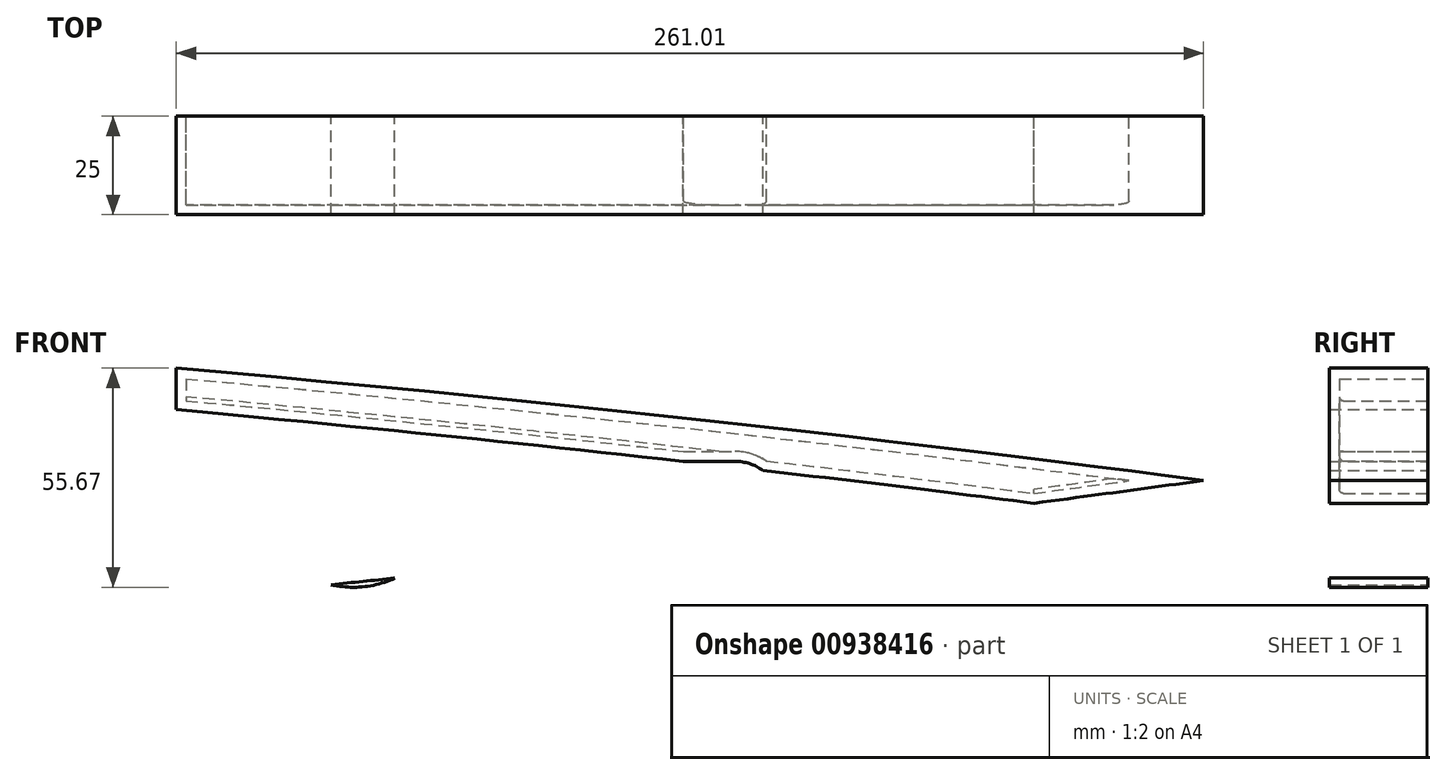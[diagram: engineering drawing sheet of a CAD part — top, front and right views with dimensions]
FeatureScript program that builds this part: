
annotation { "Feature Type Name" : "Feature", "Feature Type Description" : "" }
export const myFeature = defineFeature(function(context is Context, id is Id, definition is map)
    precondition{}
    {
        {
            var Q0;
            Q0=qCreatedBy(makeId("Front.planeOp"),FACE);
            var sketch = newSketch(context, id + "F0", { "sketchPlane" : qUnion([Q0])});
            skLineSegment(sketch, "E0", {"start": v(0, 0) * mm, "end": v(830, 0) * mm});
            skLineSegment(sketch, "E1", {"start": v(23.53, 0) * mm, "end": v(23.53, 22.98) * mm, "construction": true});
            skLineSegment(sketch, "E2", {"start": v(30.64, 0) * mm, "end": v(30.64, 25.86) * mm, "construction": true});
            skLineSegment(sketch, "E3", {"start": v(38.65, 0) * mm, "end": v(38.65, 28.62) * mm, "construction": true});
            skLineSegment(sketch, "E4", {"start": v(47.54, 0) * mm, "end": v(47.54, 31.24) * mm, "construction": true});
            skLineSegment(sketch, "E5", {"start": v(57.28, 0) * mm, "end": v(57.28, 33.72) * mm, "construction": true});
            skLineSegment(sketch, "E6", {"start": v(67.86, 0) * mm, "end": v(67.86, 36.05) * mm, "construction": true});
            skLineSegment(sketch, "E7", {"start": v(79.26, 0) * mm, "end": v(79.26, 38.22) * mm, "construction": true});
            skLineSegment(sketch, "E8", {"start": v(91.44, 0) * mm, "end": v(91.44, 40.22) * mm, "construction": true});
            skLineSegment(sketch, "E9", {"start": v(104.37, 0) * mm, "end": v(104.37, 42.04) * mm, "construction": true});
            skLineSegment(sketch, "E10", {"start": v(118.03, 0) * mm, "end": v(118.03, 43.68) * mm, "construction": true});
            skLineSegment(sketch, "E11", {"start": v(132.38, 0) * mm, "end": v(132.38, 45.13) * mm, "construction": true});
            skLineSegment(sketch, "E12", {"start": v(147.4, 0) * mm, "end": v(147.4, 46.38) * mm, "construction": true});
            skLineSegment(sketch, "E13", {"start": v(163.03, 0) * mm, "end": v(163.03, 47.45) * mm, "construction": true});
            skLineSegment(sketch, "E14", {"start": v(179.25, 0) * mm, "end": v(179.25, 48.31) * mm, "construction": true});
            skLineSegment(sketch, "E15", {"start": v(196.03, 0) * mm, "end": v(196.03, 48.98) * mm, "construction": true});
            skLineSegment(sketch, "E16", {"start": v(213.32, 0) * mm, "end": v(213.32, 49.45) * mm, "construction": true});
            skLineSegment(sketch, "E17", {"start": v(231.08, 0) * mm, "end": v(231.08, 49.73) * mm, "construction": true});
            skLineSegment(sketch, "E18", {"start": v(249.26, 0) * mm, "end": v(249.26, 49.81) * mm, "construction": true});
            skLineSegment(sketch, "E19", {"start": v(267.84, 0) * mm, "end": v(267.84, 49.72) * mm, "construction": true});
            skLineSegment(sketch, "E20", {"start": v(0.48, 0) * mm, "end": v(0.48, 3.54) * mm, "construction": true});
            skLineSegment(sketch, "E21", {"start": v(1.94, 0) * mm, "end": v(1.94, 7) * mm, "construction": true});
            skLineSegment(sketch, "E22", {"start": v(4.35, 0) * mm, "end": v(4.35, 10.38) * mm, "construction": true});
            skLineSegment(sketch, "E23", {"start": v(7.73, 0) * mm, "end": v(7.73, 13.67) * mm, "construction": true});
            skLineSegment(sketch, "E24", {"start": v(12.06, 0) * mm, "end": v(12.06, 16.87) * mm, "construction": true});
            skLineSegment(sketch, "E25", {"start": v(17.33, 0) * mm, "end": v(17.33, 19.98) * mm, "construction": true});
            skLineSegment(sketch, "E26", {"start": v(286.76, 0) * mm, "end": v(286.76, 49.45) * mm, "construction": true});
            skLineSegment(sketch, "E27", {"start": v(305.98, 0) * mm, "end": v(305.98, 49) * mm, "construction": true});
            skLineSegment(sketch, "E28", {"start": v(325.45, 0) * mm, "end": v(325.45, 48.4) * mm, "construction": true});
            skLineSegment(sketch, "E29", {"start": v(345.13, 0) * mm, "end": v(345.13, 47.64) * mm, "construction": true});
            skLineSegment(sketch, "E30", {"start": v(364.98, 0) * mm, "end": v(364.98, 46.75) * mm, "construction": true});
            skLineSegment(sketch, "E31", {"start": v(384.94, 0) * mm, "end": v(384.94, 45.71) * mm, "construction": true});
            skLineSegment(sketch, "E32", {"start": v(404.97, 0) * mm, "end": v(404.97, 44.56) * mm, "construction": true});
            skLineSegment(sketch, "E33", {"start": v(425.03, 0) * mm, "end": v(425.03, 43.3) * mm, "construction": true});
            skLineSegment(sketch, "E34", {"start": v(445.06, 0) * mm, "end": v(445.06, 41.93) * mm, "construction": true});
            skLineSegment(sketch, "E35", {"start": v(465.02, 0) * mm, "end": v(465.02, 40.47) * mm, "construction": true});
            skLineSegment(sketch, "E36", {"start": v(484.87, 0) * mm, "end": v(484.87, 38.94) * mm, "construction": true});
            skLineSegment(sketch, "E37", {"start": v(504.55, 0) * mm, "end": v(504.55, 37.33) * mm, "construction": true});
            skLineSegment(sketch, "E38", {"start": v(524.02, 0) * mm, "end": v(524.02, 35.67) * mm, "construction": true});
            skLineSegment(sketch, "E39", {"start": v(543.24, 0) * mm, "end": v(543.24, 33.96) * mm, "construction": true});
            skLineSegment(sketch, "E40", {"start": v(562.16, 0) * mm, "end": v(562.16, 32.21) * mm, "construction": true});
            skLineSegment(sketch, "E41", {"start": v(580.74, 0) * mm, "end": v(580.74, 30.44) * mm, "construction": true});
            skLineSegment(sketch, "E42", {"start": v(598.92, 0) * mm, "end": v(598.92, 28.64) * mm, "construction": true});
            skLineSegment(sketch, "E43", {"start": v(633.97, 0) * mm, "end": v(633.97, 25.03) * mm, "construction": true});
            skLineSegment(sketch, "E44", {"start": v(616.68, 0) * mm, "end": v(616.68, 26.83) * mm, "construction": true});
            skLineSegment(sketch, "E45", {"start": v(650.75, 0) * mm, "end": v(650.75, 23.23) * mm, "construction": true});
            skLineSegment(sketch, "E46", {"start": v(666.97, 0) * mm, "end": v(666.97, 21.44) * mm, "construction": true});
            skLineSegment(sketch, "E47", {"start": v(682.6, 0) * mm, "end": v(682.6, 19.68) * mm, "construction": true});
            skLineSegment(sketch, "E48", {"start": v(697.62, 0) * mm, "end": v(697.62, 17.96) * mm, "construction": true});
            skLineSegment(sketch, "E49", {"start": v(711.97, 0) * mm, "end": v(711.97, 16.27) * mm, "construction": true});
            skLineSegment(sketch, "E50", {"start": v(725.63, 0) * mm, "end": v(725.63, 14.64) * mm, "construction": true});
            skLineSegment(sketch, "E51", {"start": v(738.56, 0) * mm, "end": v(738.56, 13.06) * mm, "construction": true});
            skLineSegment(sketch, "E52", {"start": v(750.74, 0) * mm, "end": v(750.74, 11.55) * mm, "construction": true});
            skLineSegment(sketch, "E53", {"start": v(762.14, 0) * mm, "end": v(762.14, 10.11) * mm, "construction": true});
            skLineSegment(sketch, "E54", {"start": v(791.35, 0) * mm, "end": v(791.35, 6.32) * mm, "construction": true});
            skLineSegment(sketch, "E55", {"start": v(799.36, 0) * mm, "end": v(799.36, 5.25) * mm, "construction": true});
            skLineSegment(sketch, "E56", {"start": v(806.47, 0) * mm, "end": v(806.47, 4.29) * mm, "construction": true});
            skLineSegment(sketch, "E57", {"start": v(782.46, 0) * mm, "end": v(782.46, 7.49) * mm, "construction": true});
            skLineSegment(sketch, "E58", {"start": v(812.67, 0) * mm, "end": v(812.67, 3.45) * mm, "construction": true});
            skLineSegment(sketch, "E59", {"start": v(817.94, 0) * mm, "end": v(817.94, 2.72) * mm, "construction": true});
            skLineSegment(sketch, "E60", {"start": v(822.27, 0) * mm, "end": v(822.27, 2.12) * mm, "construction": true});
            skLineSegment(sketch, "E61", {"start": v(825.65, 0) * mm, "end": v(825.65, 1.65) * mm, "construction": true});
            skLineSegment(sketch, "E62", {"start": v(828.06, 0) * mm, "end": v(828.06, 1.32) * mm, "construction": true});
            skLineSegment(sketch, "E63", {"start": v(772.72, 0) * mm, "end": v(772.72, 8.76) * mm, "construction": true});
            skLineSegment(sketch, "E64", {"start": v(829.52, 0) * mm, "end": v(829.52, 1.11) * mm, "construction": true});
            skLineSegment(sketch, "E65", {"start": v(830, 0) * mm, "end": v(830, 1.05) * mm});
            skFitSpline(sketch, "E66", {"points": [v(0, 0) * mm, v(0.48, 3.54) * mm, v(1.94, 7) * mm, v(4.35, 10.38) * mm, v(7.73, 13.67) * mm, v(12.06, 16.87) * mm, v(17.33, 19.98) * mm, v(23.53, 22.98) * mm, v(30.64, 25.86) * mm, v(38.65, 28.62) * mm, v(47.54, 31.24) * mm, v(57.28, 33.72) * mm, v(67.86, 36.05) * mm, v(79.26, 38.22) * mm, v(91.44, 40.22) * mm, v(104.37, 42.04) * mm, v(118.03, 43.68) * mm, v(132.38, 45.13) * mm, v(147.4, 46.39) * mm, v(163.03, 47.45) * mm, v(179.25, 48.31) * mm, v(196.03, 48.98) * mm, v(213.32, 49.45) * mm, v(231.08, 49.73) * mm, v(249.26, 49.81) * mm, v(267.84, 49.72) * mm, v(286.76, 49.45) * mm, v(305.98, 49) * mm, v(325.45, 48.4) * mm, v(345.13, 47.64) * mm, v(364.98, 46.75) * mm, v(384.94, 45.71) * mm, v(404.97, 44.56) * mm, v(425.03, 43.3) * mm, v(445.06, 41.93) * mm, v(465.02, 40.47) * mm, v(484.87, 38.94) * mm, v(504.55, 37.33) * mm, v(524.02, 35.67) * mm, v(543.24, 33.96) * mm, v(562.16, 32.21) * mm, v(580.74, 30.44) * mm, v(598.92, 28.64) * mm, v(616.68, 26.83) * mm, v(633.97, 25.03) * mm, v(650.75, 23.23) * mm, v(666.97, 21.44) * mm, v(682.6, 19.68) * mm, v(697.62, 17.96) * mm, v(711.97, 16.27) * mm, v(725.63, 14.64) * mm, v(738.56, 13.06) * mm, v(750.74, 11.55) * mm, v(762.14, 10.11) * mm, v(772.72, 8.76) * mm, v(782.46, 7.49) * mm, v(791.35, 6.32) * mm, v(799.36, 5.25) * mm, v(806.47, 4.29) * mm, v(812.67, 3.45) * mm, v(817.94, 2.72) * mm, v(822.27, 2.12) * mm, v(825.65, 1.65) * mm, v(828.06, 1.32) * mm, v(829.52, 1.11) * mm, v(830, 1.05) * mm], "startDerivative": vector(34.1, 427.03) * mm, "endDerivative": vector(137.1, -19.25) * mm});
            skFitSpline(sketch, "E67.MirrorCS", {"points": [v(0, 0) * mm, v(0.48, -3.54) * mm, v(1.94, -7) * mm, v(4.35, -10.38) * mm, v(7.73, -13.67) * mm, v(12.06, -16.87) * mm, v(17.33, -19.98) * mm, v(23.53, -22.98) * mm, v(30.64, -25.86) * mm, v(38.65, -28.62) * mm, v(47.54, -31.24) * mm, v(57.28, -33.72) * mm, v(67.86, -36.05) * mm, v(79.26, -38.22) * mm, v(91.44, -40.22) * mm, v(104.37, -42.04) * mm, v(118.03, -43.68) * mm, v(132.38, -45.13) * mm, v(147.4, -46.39) * mm, v(163.03, -47.45) * mm, v(179.25, -48.31) * mm, v(196.03, -48.98) * mm, v(213.32, -49.45) * mm, v(231.08, -49.73) * mm, v(249.26, -49.81) * mm, v(267.84, -49.72) * mm, v(286.76, -49.45) * mm, v(305.98, -49) * mm, v(325.45, -48.4) * mm, v(345.13, -47.64) * mm, v(364.98, -46.75) * mm, v(384.94, -45.71) * mm, v(404.97, -44.56) * mm, v(425.03, -43.3) * mm, v(445.06, -41.93) * mm, v(465.02, -40.47) * mm, v(484.87, -38.94) * mm, v(504.55, -37.33) * mm, v(524.02, -35.67) * mm, v(543.24, -33.96) * mm, v(562.16, -32.21) * mm, v(580.74, -30.44) * mm, v(598.92, -28.64) * mm, v(616.68, -26.83) * mm, v(633.97, -25.03) * mm, v(650.75, -23.23) * mm, v(666.97, -21.44) * mm, v(682.6, -19.68) * mm, v(697.62, -17.96) * mm, v(711.97, -16.27) * mm, v(725.63, -14.64) * mm, v(738.56, -13.06) * mm, v(750.74, -11.55) * mm, v(762.14, -10.11) * mm, v(772.72, -8.76) * mm, v(782.46, -7.49) * mm, v(791.35, -6.32) * mm, v(799.36, -5.25) * mm, v(806.47, -4.29) * mm, v(812.67, -3.45) * mm, v(817.94, -2.72) * mm, v(822.27, -2.12) * mm, v(825.65, -1.65) * mm, v(828.06, -1.32) * mm, v(829.52, -1.11) * mm, v(830, -1.05) * mm], "startDerivative": vector(34.1, -427.03) * mm, "endDerivative": vector(137.1, 19.25) * mm});
            skLineSegment(sketch, "E68.MirrorCS", {"start": v(830, 0) * mm, "end": v(830, -1.05) * mm});
            skLineSegment(sketch, "E69", {"start": v(163.03, 47.45) * mm, "end": v(163.03, -47.45) * mm});
            skLineSegment(sketch, "E70", {"start": v(204.25, -49.23) * mm, "end": v(204.25, -33.23) * mm});
            skLineSegment(sketch, "E71", {"start": v(204.25, -33.23) * mm, "end": v(179.25, -33.23) * mm});
            skLineSegment(sketch, "E72", {"start": v(179.25, -33.23) * mm, "end": v(179.25, 33.23) * mm});
            skLineSegment(sketch, "E73", {"start": v(179.25, 33.23) * mm, "end": v(204.25, 33.23) * mm});
            skLineSegment(sketch, "E74", {"start": v(204.25, 33.23) * mm, "end": v(204.25, 49.23) * mm});
            skLineSegment(sketch, "E75", {"start": v(524.02, 35.67) * mm, "end": v(524.02, -35.67) * mm});
            skLineSegment(sketch, "E76", {"start": v(479.55, -39.36) * mm, "end": v(479.55, -23.36) * mm});
            skLineSegment(sketch, "E77", {"start": v(479.55, -23.36) * mm, "end": v(504.55, -23.36) * mm});
            skLineSegment(sketch, "E78", {"start": v(504.55, -23.36) * mm, "end": v(504.55, 23.36) * mm});
            skLineSegment(sketch, "E79", {"start": v(504.55, 23.36) * mm, "end": v(479.55, 23.36) * mm});
            skLineSegment(sketch, "E80", {"start": v(479.55, 23.36) * mm, "end": v(479.55, 39.36) * mm});
            skEllipse(sketch, "E81", {"center": v(240.25, 0) * mm, "majorRadius": 36.5 * mm, "minorRadius": 30 * mm, "majorAxis": v(1, 0)});
            skEllipse(sketch, "E82.1.0.0", {"center": v(333.25, 0) * mm, "majorRadius": 36.5 * mm, "minorRadius": 30 * mm, "majorAxis": v(1, 0)});
            skLineSegment(sketch, "E82.direction1", {"start": v(240.25, 0) * mm, "end": v(333.25, 0) * mm, "construction": true});
            skEllipse(sketch, "E83", {"center": v(425.03, 0) * mm, "majorRadius": 28 * mm, "minorRadius": 36.5 * mm, "majorAxis": v(0, -1)});
            skFitSpline(sketch, "E84.0", {"points": [v(19.9, 0) * mm, v(19.93, 0.28) * mm, v(19.97, 0.77) * mm, v(20.03, 1.33) * mm, v(20.07, 1.63) * mm, v(20.1, 1.78) * mm, v(20.12, 1.85) * mm, v(20.12, 1.88) * mm, v(20.13, 1.92) * mm, v(20.16, 1.99) * mm, v(20.2, 2.1) * mm, v(20.28, 2.3) * mm, v(20.43, 2.58) * mm, v(20.63, 2.94) * mm, v(20.87, 3.32) * mm, v(21.13, 3.7) * mm, v(21.53, 4.23) * mm, v(22.12, 4.91) * mm, v(22.98, 5.8) * mm, v(24.01, 6.71) * mm, v(25.19, 7.65) * mm, v(26.5, 8.6) * mm, v(28.4, 9.86) * mm, v(31.06, 11.42) * mm, v(34.64, 13.25) * mm, v(38.55, 15) * mm, v(44.15, 17.24) * mm, v(51.77, 19.86) * mm, v(61.74, 22.7) * mm, v(72.4, 25.26) * mm, v(83.62, 27.56) * mm, v(95.37, 29.62) * mm, v(107.56, 31.45) * mm, v(124.36, 33.6) * mm, v(146.26, 35.8) * mm, v(173.73, 37.69) * mm, v(202.17, 38.91) * mm, v(231.43, 39.53) * mm, v(261.35, 39.6) * mm, v(291.8, 39.18) * mm, v(322.69, 38.31) * mm, v(364.28, 36.62) * mm, v(416.8, 33.63) * mm, v(479.93, 28.95) * mm, v(531.98, 24.38) * mm, v(572.9, 20.44) * mm, v(603.14, 17.37) * mm, v(632.79, 14.2) * mm, v(661.73, 10.99) * mm, v(689.84, 7.73) * mm, v(716.93, 4.47) * mm, v(738.52, 1.78) * mm, v(755.07, -0.33) * mm, v(767.08, -1.9) * mm, v(778.65, -3.43) * mm, v(789.72, -4.91) * mm, v(800.24, -6.35) * mm, v(810.11, -7.7) * mm, v(817.7, -8.77) * mm, v(823.32, -9.57) * mm, v(826.6, -10.03) * mm, v(829.07, -10.39) * mm, v(830.84, -10.64) * mm, v(832.51, -10.88) * mm, v(834.08, -11.1) * mm, v(835.26, -11.27) * mm, v(836.14, -11.4) * mm, v(836.78, -11.5) * mm, v(837.37, -11.58) * mm, v(837.78, -11.64) * mm, v(838.05, -11.68) * mm, v(838.28, -11.71) * mm, v(838.4, -11.73) * mm, v(838.5, -11.74) * mm]});
            skFitSpline(sketch, "E85.MirrorCS", {"points": [v(19.9, 0) * mm, v(19.93, -0.28) * mm, v(19.97, -0.77) * mm, v(20.03, -1.33) * mm, v(20.08, -1.63) * mm, v(20.1, -1.78) * mm, v(20.12, -1.85) * mm, v(20.13, -1.87) * mm, v(20.14, -1.92) * mm, v(20.16, -1.99) * mm, v(20.2, -2.1) * mm, v(20.29, -2.29) * mm, v(20.44, -2.58) * mm, v(20.64, -2.94) * mm, v(20.88, -3.31) * mm, v(21.15, -3.7) * mm, v(21.55, -4.22) * mm, v(22.13, -4.9) * mm, v(23, -5.78) * mm, v(24.04, -6.7) * mm, v(25.22, -7.63) * mm, v(26.52, -8.57) * mm, v(28.44, -9.83) * mm, v(31.1, -11.38) * mm, v(34.7, -13.2) * mm, v(38.6, -14.93) * mm, v(44.21, -17.15) * mm, v(51.85, -19.74) * mm, v(61.83, -22.54) * mm, v(72.49, -25.06) * mm, v(83.73, -27.32) * mm, v(95.48, -29.34) * mm, v(107.68, -31.12) * mm, v(124.49, -33.22) * mm, v(146.4, -35.32) * mm, v(173.87, -37.11) * mm, v(202.32, -38.23) * mm, v(231.57, -38.74) * mm, v(261.5, -38.7) * mm, v(291.95, -38.16) * mm, v(322.83, -37.18) * mm, v(364.42, -35.33) * mm, v(416.93, -32.14) * mm, v(480.03, -27.22) * mm, v(532.07, -22.46) * mm, v(572.98, -18.36) * mm, v(603.2, -15.18) * mm, v(632.84, -11.91) * mm, v(661.77, -8.58) * mm, v(689.86, -5.22) * mm, v(716.95, -1.86) * mm, v(738.52, 0.91) * mm, v(755.06, 3.1) * mm, v(767.06, 4.7) * mm, v(778.63, 6.27) * mm, v(789.7, 7.8) * mm, v(800.21, 9.27) * mm, v(810.08, 10.67) * mm, v(817.67, 11.77) * mm, v(823.28, 12.58) * mm, v(826.56, 13.06) * mm, v(829.03, 13.42) * mm, v(830.8, 13.68) * mm, v(832.47, 13.93) * mm, v(834.03, 14.16) * mm, v(835.21, 14.33) * mm, v(836.1, 14.46) * mm, v(836.73, 14.56) * mm, v(837.32, 14.64) * mm, v(837.73, 14.7) * mm, v(838, 14.75) * mm, v(838.23, 14.78) * mm, v(838.36, 14.8) * mm, v(838.45, 14.81) * mm]});
            skLineSegment(sketch, "E86", {"start": v(100.03, 30.3) * mm, "end": v(134.03, 30.3) * mm});
            skLineSegment(sketch, "E87", {"start": v(140.03, 24.3) * mm, "end": v(140.03, -24.26) * mm});
            skLineSegment(sketch, "E88", {"start": v(133.98, -30.26) * mm, "end": v(100.03, -29.99) * mm});
            skPoint(sketch, "E89.visualSharp", {"position": v(140.03, 30.3) * mm});
            skArc(sketch, "E89.filletArc", {"start": v(140.03, 24.3) * mm, "mid": v(138.27, 28.55) * mm, "end": v(134.03, 30.3) * mm});
            skPoint(sketch, "E90.visualSharp", {"position": v(140.03, -30.3) * mm});
            skArc(sketch, "E90.filletArc", {"start": v(133.98, -30.26) * mm, "mid": v(138.25, -28.52) * mm, "end": v(140.03, -24.26) * mm});
            skEllipse(sketch, "E91", {"center": v(569.02, 0) * mm, "majorRadius": 20 * mm, "minorRadius": 22.5 * mm, "majorAxis": v(0, -1)});
            skLineSegment(sketch, "E92.bottom", {"start": v(625.97, -12) * mm, "end": v(665.97, -12) * mm});
            skLineSegment(sketch, "E92.top", {"start": v(625.97, 12) * mm, "end": v(665.97, 12) * mm});
            skLineSegment(sketch, "E92.left", {"start": v(623.97, -10) * mm, "end": v(623.97, 10) * mm});
            skLineSegment(sketch, "E92.right", {"start": v(665.97, -12) * mm, "end": v(665.97, 12) * mm});
            skPoint(sketch, "E92.middle", {"position": v(644.97, 0) * mm});
            skArc(sketch, "E93", {"start": v(665.97, 12) * mm, "mid": v(677.97, 0) * mm, "end": v(665.97, -12) * mm});
            skPoint(sketch, "E94.visualSharp", {"position": v(623.97, 12) * mm});
            skArc(sketch, "E94.filletArc", {"start": v(625.97, 12) * mm, "mid": v(624.56, 11.41) * mm, "end": v(623.97, 10) * mm});
            skPoint(sketch, "E95.visualSharp", {"position": v(623.97, -12) * mm});
            skArc(sketch, "E95.filletArc", {"start": v(623.97, -10) * mm, "mid": v(624.56, -11.41) * mm, "end": v(625.97, -12) * mm});
            skPoint(sketch, "E96", {"position": v(276.75, 0) * mm});
            skPoint(sketch, "E97", {"position": v(296.75, 0) * mm});
            skLineSegment(sketch, "E98.bottom", {"start": v(276.26, 65.67) * mm, "end": v(297.26, 65.67) * mm});
            skLineSegment(sketch, "E98.top", {"start": v(276.26, 33.23) * mm, "end": v(297.26, 33.23) * mm});
            skLineSegment(sketch, "E98.left", {"start": v(276.26, 65.67) * mm, "end": v(276.26, 33.23) * mm});
            skLineSegment(sketch, "E98.right", {"start": v(297.26, 65.67) * mm, "end": v(297.26, 33.23) * mm});
            skPoint(sketch, "E99", {"position": v(369.75, 0) * mm});
            skPoint(sketch, "E100", {"position": v(388.53, 0) * mm});
            skLineSegment(sketch, "E101", {"start": v(379.14, 0) * mm, "end": v(379.14, 46.03) * mm, "construction": true});
            skLineSegment(sketch, "E102.bottom", {"start": v(368.64, 58.81) * mm, "end": v(389.64, 58.81) * mm});
            skLineSegment(sketch, "E102.top", {"start": v(368.64, 33.23) * mm, "end": v(389.64, 33.23) * mm});
            skLineSegment(sketch, "E102.left", {"start": v(368.64, 58.81) * mm, "end": v(368.64, 33.23) * mm});
            skLineSegment(sketch, "E102.right", {"start": v(389.64, 58.81) * mm, "end": v(389.64, 33.23) * mm});
            skLineSegment(sketch, "E103.MirrorCS", {"start": v(297.26, -65.67) * mm, "end": v(297.26, -33.23) * mm});
            skLineSegment(sketch, "E104.MirrorCS", {"start": v(276.26, -65.67) * mm, "end": v(297.26, -65.67) * mm});
            skLineSegment(sketch, "E105.MirrorCS", {"start": v(276.26, -65.67) * mm, "end": v(276.26, -33.23) * mm});
            skLineSegment(sketch, "E106.MirrorCS", {"start": v(276.26, -33.23) * mm, "end": v(297.26, -33.23) * mm});
            skLineSegment(sketch, "E107.MirrorCS", {"start": v(368.64, -58.81) * mm, "end": v(389.64, -58.81) * mm});
            skLineSegment(sketch, "E108.MirrorCS", {"start": v(368.64, -58.81) * mm, "end": v(368.64, -33.23) * mm});
            skLineSegment(sketch, "E109.MirrorCS", {"start": v(389.64, -58.81) * mm, "end": v(389.64, -33.23) * mm});
            skLineSegment(sketch, "E110.MirrorCS", {"start": v(368.64, -33.23) * mm, "end": v(389.64, -33.23) * mm});
            skSolve(sketch);
        }
        {
            var Q0;
            {var subQ5=sQuery(id+"F0.wireOp",EDGE,"E84.0");Q0=makeQuery(id+"F0.imprint","IMPRINT",FACE,{"disambiguationData":[TD([[makeQuery(id+"F0.imprint","IMPRINT",EDGE,{"derivedFrom":subQ5}),1.0]])]});}
            var Q1;
            {var subQ6=sQuery(id+"F0.wireOp",EDGE,"E85.MirrorCS");Q1=makeQuery(id+"F0.imprint","IMPRINT",FACE,{"disambiguationData":[TD([[makeQuery(id+"F0.imprint","IMPRINT",EDGE,{"derivedFrom":subQ6}),-1.0]])]});}
            extrude(context, id + "F1", {"entities" : qUnion([Q0, Q1]), "endBound" : BoundingType.SYMMETRIC, "depth" : 25 * mm, "offsetDistance" : 25 * mm});
        }
        {
            var Q0;
            Q0=makeQuery(id+"F1.opExtrude","CAP_FACE",FACE,{"disambiguationData":[OSD([sQuery(id+"F0.wireOp",EDGE,"E66"),sQuery(id+"F0.wireOp",EDGE,"E67.MirrorCS"),sQuery(id+"F0.wireOp",EDGE,"E69"),sQuery(id+"F0.wireOp",EDGE,"E84.0"),sQuery(id+"F0.wireOp",EDGE,"E85.MirrorCS"),sQuery(id+"F0.wireOp",EDGE,"E86"),sQuery(id+"F0.wireOp",EDGE,"E87"),sQuery(id+"F0.wireOp",EDGE,"E88"),sQuery(id+"F0.wireOp",EDGE,"E89.filletArc"),sQuery(id+"F0.wireOp",EDGE,"E90.filletArc")])],"isStart":true});
            shell(context, id + "F2", {"entities" : qUnion([Q0]), "thickness" : 2.5 * mm});
        }
        {
            var Q0;
            {var subQ0=sQuery(id+"F0.wireOp",EDGE,"E86");Q0=makeQuery(id+"F2.opShell","OFFSET_EDGE",EDGE,{"disambiguationData":[OSD([subQ0]),TDD([makeQuery(id+"F1.opExtrude","CAP_EDGE",EDGE,{"disambiguationData":[OSD([subQ0])],"isStart":false})])]});}
            var Q1;
            {var subQ0=sQuery(id+"F0.wireOp",EDGE,"E84.0");Q1=makeQuery(id+"F2.opShell","OFFSET_EDGE",EDGE,{"disambiguationData":[OSD([subQ0]),TDD([makeQuery(id+"F1.opExtrude","CAP_EDGE",EDGE,{"disambiguationData":[OSD([subQ0])],"isStart":false})])]});}
            var Q2;
            {var subQ0=sQuery(id+"F0.wireOp",EDGE,"E85.MirrorCS");Q2=makeQuery(id+"F2.opShell","OFFSET_EDGE",EDGE,{"disambiguationData":[OSD([subQ0]),TDD([makeQuery(id+"F1.opExtrude","CAP_EDGE",EDGE,{"disambiguationData":[OSD([subQ0])],"isStart":false})])]});}
            fillet(context, id + "F3", {"entities" : qUnion([Q0, Q1, Q2]), "radius" : 1 * mm, "tangentPropagation" : true, "allowEdgeOverflow" : false});
        }
    });
